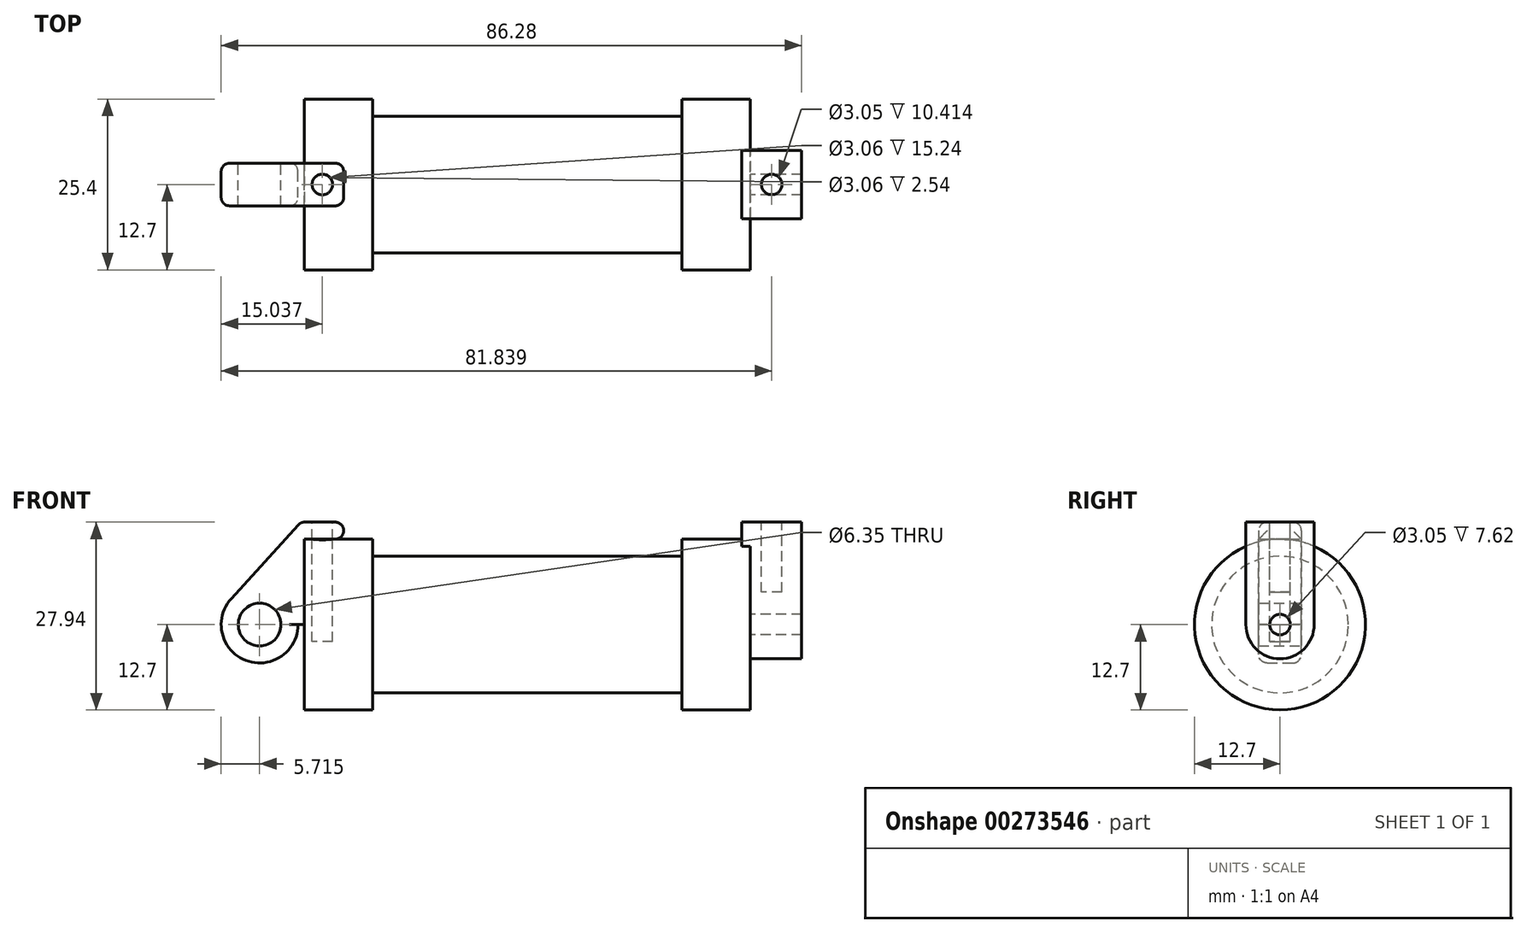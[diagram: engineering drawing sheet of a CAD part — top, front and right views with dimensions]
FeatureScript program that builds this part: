
annotation { "Feature Type Name" : "Feature", "Feature Type Description" : "" }
export const myFeature = defineFeature(function(context is Context, id is Id, definition is map)
    precondition{}
    {
        {
            var Q0;
            Q0=qCreatedBy(makeId("Front.planeOp"),FACE);
            var sketch = newSketch(context, id + "F0", { "sketchPlane" : qUnion([Q0])});
            skLineSegment(sketch, "E0", {"start": v(0, 0) * mm, "end": v(0, 12.7) * mm});
            skLineSegment(sketch, "E1", {"start": v(0, 12.7) * mm, "end": v(10.16, 12.7) * mm});
            skLineSegment(sketch, "E2", {"start": v(10.16, 12.7) * mm, "end": v(10.16, 10.16) * mm});
            skLineSegment(sketch, "E3", {"start": v(10.16, 10.16) * mm, "end": v(56.13, 10.16) * mm});
            skLineSegment(sketch, "E4", {"start": v(56.13, 10.16) * mm, "end": v(56.13, 12.7) * mm});
            skLineSegment(sketch, "E5", {"start": v(56.13, 12.7) * mm, "end": v(66.3, 12.7) * mm});
            skLineSegment(sketch, "E6", {"start": v(66.3, 12.7) * mm, "end": v(66.3, 0) * mm});
            skLineSegment(sketch, "E7", {"start": v(66.3, 0) * mm, "end": v(0, 0) * mm});
            skLineSegment(sketch, "E8", {"start": v(5.84, 15.24) * mm, "end": v(-0.5, 15.24) * mm});
            skLineSegment(sketch, "E9", {"start": v(-0.5, 15.24) * mm, "end": v(-10.88, 3.85) * mm});
            skLineSegment(sketch, "E10", {"start": v(0, 0) * mm, "end": v(-6.65, 0) * mm});
            skCircle(sketch, "E11", {"center": v(-6.65, 0) * mm, "radius": 5.72 * mm});
            skCircle(sketch, "E12", {"center": v(-6.65, 0) * mm, "radius": 3.18 * mm});
            skLineSegment(sketch, "E13", {"start": v(5.84, 15.24) * mm, "end": v(5.84, -9.4) * mm});
            skLineSegment(sketch, "E14", {"start": v(5.84, -9.4) * mm, "end": v(-8.18, -5.5) * mm});
            skLineSegment(sketch, "E15", {"start": v(0, 0) * mm, "end": v(66.3, 0) * mm, "construction": true});
            skLineSegment(sketch, "E16", {"start": v(0, 0) * mm, "end": v(66.3, 0) * mm});
            skSolve(sketch);
        }
        {
            var Q0;
            {var subQ3=sQuery(id+"F0.wireOp",EDGE,"E0");Q0=makeQuery(id+"F0.imprint","IMPRINT",FACE,{"disambiguationData":[TD([[makeQuery(id+"F0.imprint","IMPRINT",EDGE,{"derivedFrom":subQ3}),1.0]])]});}
            var Q1;
            {var subQ4=sQuery(id+"F0.wireOp",EDGE,"E12");Q1=makeQuery(id+"F0.imprint","IMPRINT",FACE,{"disambiguationData":[TD([[makeQuery(id+"F0.imprint","IMPRINT",EDGE,{"derivedFrom":subQ4}),-1.0]])]});}
            extrude(context, id + "F1", {"entities" : qUnion([Q0, Q1]), "endBound" : BoundingType.SYMMETRIC, "depth" : 6.35 * mm});
        }
        {
            var Q0;
            {var subQ0=sQuery(id+"F0.wireOp",EDGE,"E0");Q0=makeQuery(id+"F0.imprint","IMPRINT",FACE,{"disambiguationData":[TD([[makeQuery(id+"F0.imprint","IMPRINT",EDGE,{"derivedFrom":subQ0}),-1.0]])]});}
            var Q1;
            {var subQ0=sQuery(id+"F0.wireOp",EDGE,"E2");Q1=makeQuery(id+"F0.imprint","IMPRINT",FACE,{"disambiguationData":[TD([[makeQuery(id+"F0.imprint","IMPRINT",EDGE,{"derivedFrom":subQ0}),-1.0]])]});}
            var Q2;
            Q2=sQuery(id+"F0.wireOp",EDGE,"E16");
            revolve(context, id + "F2", {"entities" : qUnion([Q0, Q1]), "axis" : qUnion([Q2]), "revolveType" : RevolveType.FULL});
        }
        {
            var Q0;
            Q0=makeQuery(id+"F2.opRevolve","SWEPT_FACE",FACE,{"disambiguationData":[OSD([sQuery(id+"F0.wireOp",EDGE,"E6")])]});
            var sketch = newSketch(context, id + "F3", { "sketchPlane" : qUnion([Q0])});
            skCircle(sketch, "E17", {"center": v(0, 0) * mm, "radius": 1.52 * mm});
            skCircle(sketch, "E18", {"center": v(0, 0) * mm, "radius": 5.08 * mm});
            skLineSegment(sketch, "E19", {"start": v(-12.7, 0) * mm, "end": v(12.7, 0) * mm, "construction": true});
            skLineSegment(sketch, "E20", {"start": v(-5.08, 0) * mm, "end": v(-5.08, 15.24) * mm});
            skLineSegment(sketch, "E21", {"start": v(5.08, 0) * mm, "end": v(5.08, 15.24) * mm});
            skLineSegment(sketch, "E22", {"start": v(-5.08, 15.24) * mm, "end": v(5.08, 15.24) * mm});
            skSolve(sketch);
        }
        {
            var Q0;
            {var subQ0=sQuery(id+"F3.wireOp",EDGE,"E20");var subQ1=sQuery(id+"F3.wireOp",EDGE,"E18");var subQ2=makeQuery(id+"F3.imprint","INTERSECT",VERTEX,{"derivedFrom":[subQ1,subQ0]});Q0=makeQuery(id+"F3.imprint","IMPRINT",FACE,{"disambiguationData":[TD([[makeQuery(id+"F3.imprint","IMPRINT",EDGE,{"disambiguationData":[TD([[subQ2,1.0]])],"derivedFrom":subQ1}),-1.0]])]});}
            var Q1;
            Q1=makeQuery(id+"F3.imprint","IMPRINT",FACE,{"disambiguationData":[TD([[makeQuery(id+"F3.imprint","IMPRINT",EDGE,{"derivedFrom":sQuery(id+"F3.wireOp",EDGE,"E17")}),-1.0]])]});
            var Q2;
            {var subQ0=sQuery(id+"F3.wireOp",EDGE,"E22");Q2=makeQuery(id+"F3.imprint","IMPRINT",FACE,{"disambiguationData":[TD([[makeQuery(id+"F3.imprint","IMPRINT",EDGE,{"derivedFrom":subQ0}),-1.0]])]});}
            extrude(context, id + "F4", {"entities" : qUnion([Q0, Q1, Q2]), "operationType" : NewBodyOperationType.ADD, "depth" : 7.62 * mm});
        }
        {
            var Q0;
            Q0=makeQuery(id+"F4.opExtrude","CAP_FACE",FACE,{"disambiguationData":[OSD([sQuery(id+"F3.wireOp",EDGE,"E17"),sQuery(id+"F3.wireOp",EDGE,"E18"),sQuery(id+"F3.wireOp",EDGE,"E20"),sQuery(id+"F3.wireOp",EDGE,"E21"),sQuery(id+"F3.wireOp",EDGE,"E22")])],"isStart":true});
            extrude(context, id + "F5", {"entities" : qUnion([Q0]), "operationType" : NewBodyOperationType.ADD, "depth" : 1.27 * mm});
        }
        {
            var Q0;
            {var subQ0=sQuery(id+"F3.wireOp",EDGE,"E22");Q0=makeQuery(id+"F5.boolean.opBoolean","MERGE",FACE,{"derivedFrom":[makeQuery(id+"F4.opExtrude","SWEPT_FACE",FACE,{"disambiguationData":[OSD([subQ0])]}),makeQuery(id+"F5.opExtrude","SWEPT_FACE",FACE,{"disambiguationData":[OSD([subQ0])]})]});}
            var sketch = newSketch(context, id + "F6", { "sketchPlane" : qUnion([Q0])});
            skLineSegment(sketch, "E23", {"start": v(69.47, 5.08) * mm, "end": v(69.47, -5.08) * mm, "construction": true});
            skCircle(sketch, "E24", {"center": v(69.47, 0) * mm, "radius": 1.52 * mm});
            skSolve(sketch);
        }
        {
            var Q0;
            Q0=makeQuery(id+"F6.imprint","IMPRINT",FACE,{"disambiguationData":[TD([[makeQuery(id+"F6.imprint","IMPRINT",EDGE,{"derivedFrom":sQuery(id+"F6.wireOp",EDGE,"E24")}),1.0]])]});
            var Q1;
            Q1=sQuery(id+"F6.wireOp",EDGE,"E24");
            extrude(context, id + "F7", {"entities" : qUnion([Q0]), "operationType" : NewBodyOperationType.REMOVE, "surfaceEntities" : qUnion([Q1]), "oppositeDirection" : true, "depth" : 10.4 * mm});
        }
        {
            var Q0;
            Q0=makeQuery(id+"F1.opExtrude","SWEPT_FACE",FACE,{"disambiguationData":[OSD([sQuery(id+"F0.wireOp",EDGE,"E8")])]});
            var sketch = newSketch(context, id + "F8", { "sketchPlane" : qUnion([Q0])});
            skLineSegment(sketch, "E25", {"start": v(-0.5, 0) * mm, "end": v(5.84, 0) * mm, "construction": true});
            skCircle(sketch, "E26", {"center": v(2.67, 0) * mm, "radius": 1.53 * mm});
            skSolve(sketch);
        }
        {
            var Q0;
            Q0=makeQuery(id+"F8.imprint","IMPRINT",FACE,{"disambiguationData":[TD([[makeQuery(id+"F8.imprint","IMPRINT",EDGE,{"derivedFrom":sQuery(id+"F8.wireOp",EDGE,"E26")}),1.0]])]});
            var Q1;
            Q1=sQuery(id+"F8.wireOp",EDGE,"E26");
            extrude(context, id + "F9", {"entities" : qUnion([Q0]), "operationType" : NewBodyOperationType.REMOVE, "surfaceEntities" : qUnion([Q1]), "oppositeDirection" : true, "depth" : 17.78 * mm});
        }
        {
            var Q0;
            Q0=makeQuery(id+"F2.opRevolve","SWEPT_EDGE",EDGE,{"disambiguationData":[OSD([sQuery(id+"F0.wireOp",EDGE,"E1"),sQuery(id+"F0.wireOp",EDGE,"E2")])]});
            var Q1;
            Q1=makeQuery(id+"F2.opRevolve","SWEPT_EDGE",EDGE,{"disambiguationData":[OSD([sQuery(id+"F0.wireOp",EDGE,"E2"),sQuery(id+"F0.wireOp",EDGE,"E3")])]});
            var Q2;
            Q2=makeQuery(id+"F2.opRevolve","SWEPT_EDGE",EDGE,{"disambiguationData":[OSD([sQuery(id+"F0.wireOp",EDGE,"E0"),sQuery(id+"F0.wireOp",EDGE,"E1")])]});
            var Q3;
            Q3=makeQuery(id+"F1.opExtrude","CAP_EDGE",EDGE,{"disambiguationData":[OSD([sQuery(id+"F0.wireOp",EDGE,"E8")])],"isStart":false});
            var Q4;
            Q4=makeQuery(id+"F1.opExtrude","SWEPT_EDGE",EDGE,{"disambiguationData":[OSD([sQuery(id+"F0.wireOp",EDGE,"E8"),sQuery(id+"F0.wireOp",EDGE,"E9")])]});
            var Q5;
            Q5=makeQuery(id+"F1.opExtrude","CAP_EDGE",EDGE,{"disambiguationData":[OSD([sQuery(id+"F0.wireOp",EDGE,"E9")])],"isStart":false});
            var Q6;
            Q6=makeQuery(id+"F1.opExtrude","CAP_EDGE",EDGE,{"disambiguationData":[OSD([sQuery(id+"F0.wireOp",EDGE,"E9")])],"isStart":true});
            var Q7;
            Q7=makeQuery(id+"F1.opExtrude","CAP_EDGE",EDGE,{"disambiguationData":[OSD([sQuery(id+"F0.wireOp",EDGE,"E13")])],"isStart":false});
            var Q8;
            Q8=makeQuery(id+"F1.opExtrude","SWEPT_EDGE",EDGE,{"disambiguationData":[OSD([sQuery(id+"F0.wireOp",EDGE,"E1"),sQuery(id+"F0.wireOp",EDGE,"E13")])]});
            var Q9;
            Q9=makeQuery(id+"F1.opExtrude","SWEPT_EDGE",EDGE,{"disambiguationData":[OSD([sQuery(id+"F0.wireOp",EDGE,"E8"),sQuery(id+"F0.wireOp",EDGE,"E13")])]});
            var Q10;
            Q10=makeQuery(id+"F1.opExtrude","CAP_EDGE",EDGE,{"disambiguationData":[OSD([sQuery(id+"F0.wireOp",EDGE,"E13")])],"isStart":true});
            var Q11;
            Q11=makeQuery(id+"F1.opExtrude","CAP_EDGE",EDGE,{"disambiguationData":[OSD([sQuery(id+"F0.wireOp",EDGE,"E8")])],"isStart":true});
            var Q12;
            Q12=makeQuery(id+"F1.opExtrude","CAP_EDGE",EDGE,{"disambiguationData":[OSD([sQuery(id+"F0.wireOp",EDGE,"E11")])],"isStart":true});
            var Q13;
            Q13=makeQuery(id+"F1.opExtrude","SWEPT_EDGE",EDGE,{"disambiguationData":[OSD([sQuery(id+"F0.wireOp",EDGE,"E9"),sQuery(id+"F0.wireOp",EDGE,"E11")])]});
            var Q14;
            Q14=makeQuery(id+"F1.opExtrude","CAP_EDGE",EDGE,{"disambiguationData":[OSD([sQuery(id+"F0.wireOp",EDGE,"E11")])],"isStart":false});
            var Q15;
            Q15=makeQuery(id+"F2.opRevolve","SWEPT_EDGE",EDGE,{"disambiguationData":[OSD([sQuery(id+"F0.wireOp",EDGE,"E4"),sQuery(id+"F0.wireOp",EDGE,"E5")])]});
            var Q16;
            Q16=makeQuery(id+"F2.opRevolve","SWEPT_EDGE",EDGE,{"disambiguationData":[OSD([sQuery(id+"F0.wireOp",EDGE,"E3"),sQuery(id+"F0.wireOp",EDGE,"E4")])]});
            var Q17;
            Q17=makeQuery(id+"F4.boolean.opBoolean","SPLIT",EDGE,{"disambiguationData":[OD(1.0)],"derivedFrom":makeQuery(id+"F2.opRevolve","SWEPT_EDGE",EDGE,{"disambiguationData":[OSD([sQuery(id+"F0.wireOp",EDGE,"E5"),sQuery(id+"F0.wireOp",EDGE,"E6")])]})});
            var Q18;
            Q18=makeQuery(id+"F4.opExtrude","CAP_EDGE",EDGE,{"disambiguationData":[OSD([sQuery(id+"F3.wireOp",EDGE,"E20")])],"isStart":false});
            var Q19;
            Q19=makeQuery(id+"F4.opExtrude","CAP_EDGE",EDGE,{"disambiguationData":[OSD([sQuery(id+"F3.wireOp",EDGE,"E21")])],"isStart":false});
            var Q20;
            Q20=makeQuery(id+"F4.opExtrude","CAP_EDGE",EDGE,{"disambiguationData":[OSD([sQuery(id+"F3.wireOp",EDGE,"E18")])],"isStart":false});
            var Q21;
            Q21=makeQuery(id+"F4.opExtrude","CAP_EDGE",EDGE,{"disambiguationData":[OSD([sQuery(id+"F3.wireOp",EDGE,"E22")])],"isStart":false});
            var Q22;
            Q22=makeQuery(id+"F5.opExtrude","CAP_EDGE",EDGE,{"disambiguationData":[OSD([sQuery(id+"F3.wireOp",EDGE,"E22")])],"isStart":false});
            var Q23;
            Q23=makeQuery(id+"F5.opExtrude","CAP_EDGE",EDGE,{"disambiguationData":[OSD([sQuery(id+"F0.wireOp",EDGE,"E5"),sQuery(id+"F0.wireOp",EDGE,"E6")])],"isStart":false});
            var Q24;
            Q24=makeQuery(id+"F5.opExtrude","CAP_EDGE",EDGE,{"disambiguationData":[OSD([sQuery(id+"F3.wireOp",EDGE,"E20")])],"isStart":false});
            var Q25;
            {var subQ0=sQuery(id+"F3.wireOp",EDGE,"E22");var subQ1=sQuery(id+"F3.wireOp",EDGE,"E20");Q25=makeQuery(id+"F5.boolean.opBoolean","MERGE",EDGE,{"derivedFrom":[makeQuery(id+"F4.opExtrude","SWEPT_EDGE",EDGE,{"disambiguationData":[OSD([subQ1,subQ0])]}),makeQuery(id+"F5.opExtrude","SWEPT_EDGE",EDGE,{"disambiguationData":[OSD([subQ1,subQ0])]})]});}
            var Q26;
            Q26=makeQuery(id+"F4.opExtrude","SWEPT_EDGE",EDGE,{"disambiguationData":[OSD([sQuery(id+"F3.wireOp",EDGE,"E18"),sQuery(id+"F3.wireOp",EDGE,"E21")])]});
            var Q27;
            {var subQ0=sQuery(id+"F3.wireOp",EDGE,"E22");var subQ1=sQuery(id+"F3.wireOp",EDGE,"E21");Q27=makeQuery(id+"F5.boolean.opBoolean","MERGE",EDGE,{"derivedFrom":[makeQuery(id+"F4.opExtrude","SWEPT_EDGE",EDGE,{"disambiguationData":[OSD([subQ1,subQ0])]}),makeQuery(id+"F5.opExtrude","SWEPT_EDGE",EDGE,{"disambiguationData":[OSD([subQ1,subQ0])]})]});}
            var Q28;
            Q28=makeQuery(id+"F4.opExtrude","SWEPT_EDGE",EDGE,{"disambiguationData":[OSD([sQuery(id+"F3.wireOp",EDGE,"E18"),sQuery(id+"F3.wireOp",EDGE,"E20")])]});
            var Q29;
            Q29=makeQuery(id+"F5.opExtrude","CAP_EDGE",EDGE,{"disambiguationData":[OSD([sQuery(id+"F3.wireOp",EDGE,"E21")])],"isStart":false});
            fillet(context, id + "F10", {"entities" : qUnion([Q0, Q1, Q2, Q3, Q4, Q5, Q6, Q7, Q8, Q9, Q10, Q11, Q12, Q13, Q14, Q15, Q16, Q17, Q18, Q19, Q20, Q21, Q22, Q23, Q24, Q25, Q26, Q27, Q28, Q29]), "radius" : 1.27 * mm, "tangentPropagation" : true, "allowEdgeOverflow" : false});
        }
    });
